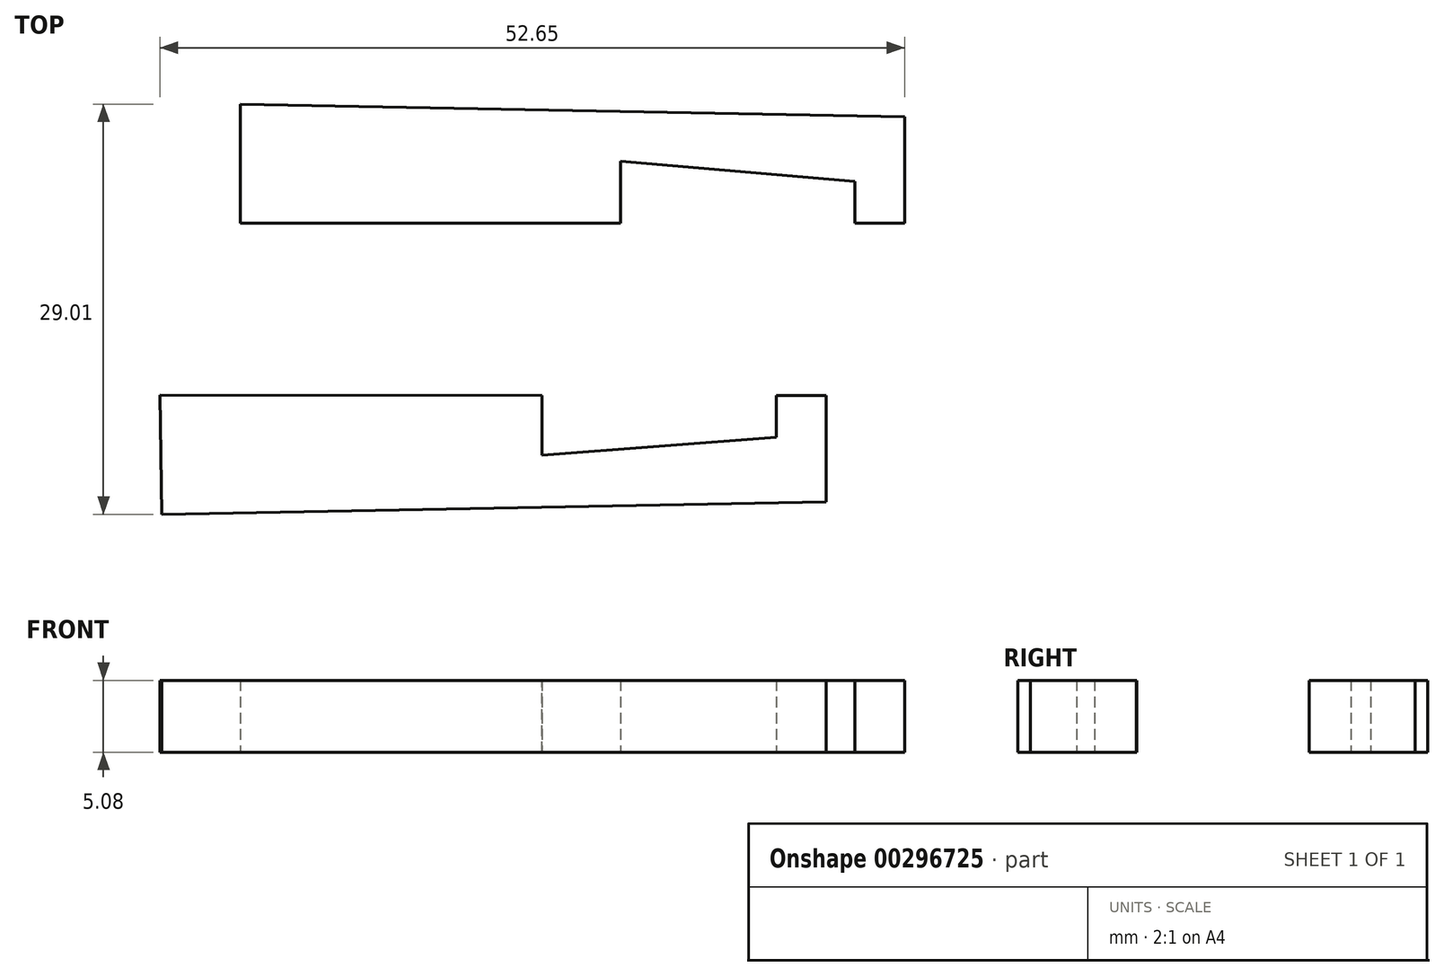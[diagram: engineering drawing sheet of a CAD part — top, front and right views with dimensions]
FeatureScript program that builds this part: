
annotation { "Feature Type Name" : "Feature", "Feature Type Description" : "" }
export const myFeature = defineFeature(function(context is Context, id is Id, definition is map)
    precondition{}
    {
        {
            var Q0;
            Q0=qCreatedBy(makeId("Top.planeOp"),FACE);
            var sketch = newSketch(context, id + "F0", { "sketchPlane" : qUnion([Q0])});
            skPoint(sketch, "E0.middle", {"position": v(0, 0) * mm});
            skLineSegment(sketch, "E1", {"start": v(18.46, 7.51) * mm, "end": v(-28.52, 8.4) * mm});
            skLineSegment(sketch, "E2", {"start": v(-1.63, 4.12) * mm, "end": v(-1.63, -0.08) * mm});
            skLineSegment(sketch, "E3", {"start": v(14.95, 2.96) * mm, "end": v(-1.63, 4.36) * mm});
            skLineSegment(sketch, "E4", {"start": v(-1.63, 4.36) * mm, "end": v(-1.63, 4.12) * mm});
            skLineSegment(sketch, "E5", {"start": v(-28.52, 0) * mm, "end": v(-1.63, 0) * mm});
            skLineSegment(sketch, "E6", {"start": v(-28.52, 0) * mm, "end": v(-28.52, 8.4) * mm});
            skLineSegment(sketch, "E7", {"start": v(-1.63, 0) * mm, "end": v(-1.63, 0) * mm});
            skLineSegment(sketch, "E8", {"start": v(18.46, 0) * mm, "end": v(18.46, 7.51) * mm});
            skLineSegment(sketch, "E9", {"start": v(14.95, 2.96) * mm, "end": v(14.95, 0) * mm});
            skLineSegment(sketch, "E10", {"start": v(14.95, 0) * mm, "end": v(18.46, 0) * mm});
            skSolve(sketch);
        }
        {
            var Q0;
            Q0=makeQuery(id+"F0.imprint","IMPRINT",FACE,{"disambiguationData":[TD([[makeQuery(id+"F0.imprint","IMPRINT",EDGE,{"derivedFrom":sQuery(id+"F0.wireOp",EDGE,"E1")}),1.0]])]});
            extrude(context, id + "F1", {"entities" : qUnion([Q0]), "depth" : 5.08 * mm});
        }
        {
            var Q0;
            Q0=qCreatedBy(makeId("Top.planeOp"),FACE);
            var sketch = newSketch(context, id + "F2", { "sketchPlane" : qUnion([Q0])});
            skLineSegment(sketch, "E11", {"start": v(-7.2, -12.2) * mm, "end": v(-7.2, -16.43) * mm});
            skLineSegment(sketch, "E12.MirrorCS", {"start": v(12.9, -19.72) * mm, "end": v(-34.08, -20.6) * mm});
            skLineSegment(sketch, "E13.MirrorCS", {"start": v(-34.19, -12.19) * mm, "end": v(-7.2, -12.2) * mm});
            skLineSegment(sketch, "E14.MirrorCS", {"start": v(9.39, -15.16) * mm, "end": v(-7.2, -16.43) * mm});
            skLineSegment(sketch, "E15.MirrorCS", {"start": v(9.39, -15.16) * mm, "end": v(9.39, -12.2) * mm});
            skLineSegment(sketch, "E16.MirrorCS", {"start": v(9.39, -12.2) * mm, "end": v(12.9, -12.2) * mm});
            skLineSegment(sketch, "E17.MirrorCS", {"start": v(12.9, -12.2) * mm, "end": v(12.9, -19.72) * mm});
            skLineSegment(sketch, "E18", {"start": v(-7.2, -12.2) * mm, "end": v(-7.2, -12.2) * mm});
            skLineSegment(sketch, "E19", {"start": v(-34.19, -12.19) * mm, "end": v(-34.08, -20.6) * mm});
            skSolve(sketch);
        }
        {
            var Q0;
            Q0 = qSketchRegion(id + "F2", true);
            extrude(context, id + "F3", {"entities" : qUnion([Q0]), "depth" : 5.08 * mm});
        }
    });
